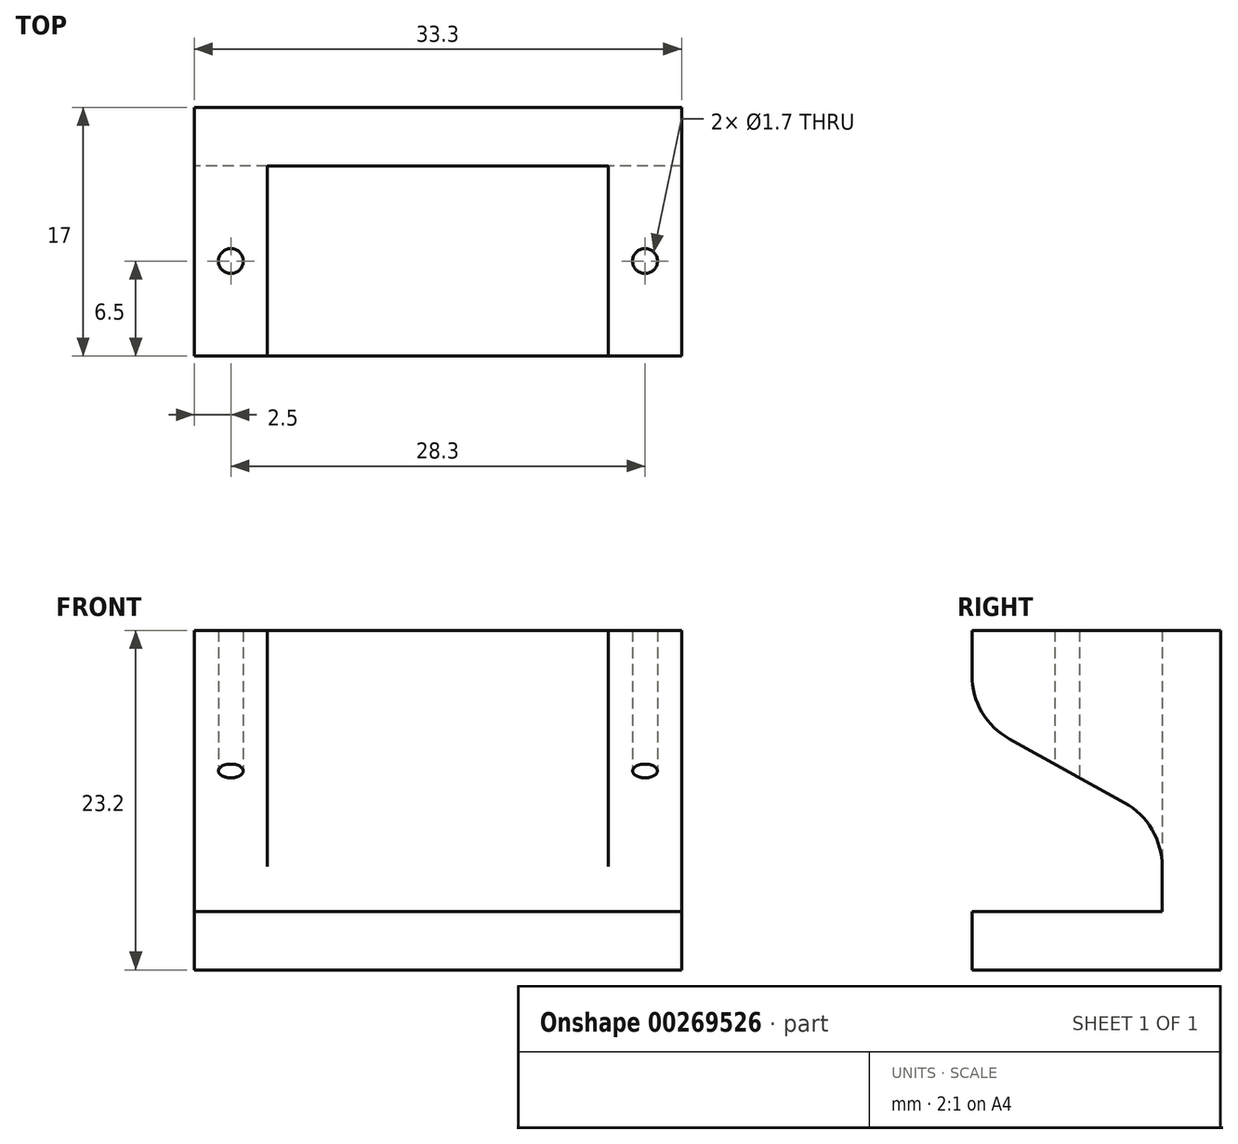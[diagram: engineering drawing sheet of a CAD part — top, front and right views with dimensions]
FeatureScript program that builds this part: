
annotation { "Feature Type Name" : "Feature", "Feature Type Description" : "" }
export const myFeature = defineFeature(function(context is Context, id is Id, definition is map)
    precondition{}
    {
        {
            var Q0;
            Q0=qCreatedBy(makeId("Top.planeOp"),FACE);
            var sketch = newSketch(context, id + "F0", { "sketchPlane" : qUnion([Q0])});
            skLineSegment(sketch, "E0.bottom", {"start": v(16.65, 8.5) * mm, "end": v(-16.65, 8.5) * mm});
            skLineSegment(sketch, "E0.top", {"start": v(16.65, -8.5) * mm, "end": v(-16.65, -8.5) * mm});
            skLineSegment(sketch, "E0.left", {"start": v(16.65, 8.5) * mm, "end": v(16.65, -8.5) * mm});
            skLineSegment(sketch, "E0.right", {"start": v(-16.65, 8.5) * mm, "end": v(-16.65, -8.5) * mm});
            skPoint(sketch, "E0.middle", {"position": v(0, 0) * mm});
            skLineSegment(sketch, "E1", {"start": v(11.65, -8.5) * mm, "end": v(11.65, 8.5) * mm});
            skLineSegment(sketch, "E2", {"start": v(-11.65, -8.5) * mm, "end": v(-11.65, 8.5) * mm});
            skLineSegment(sketch, "E3", {"start": v(-11.65, 4.5) * mm, "end": v(11.65, 4.5) * mm});
            skCircle(sketch, "E4", {"center": v(14.15, -2) * mm, "radius": 0.85 * mm});
            skCircle(sketch, "E5", {"center": v(-14.15, -2) * mm, "radius": 0.85 * mm});
            skCircle(sketch, "E6", {"center": v(-5.75, -2.2) * mm, "radius": 3.8 * mm});
            skCircle(sketch, "E7.MirrorC", {"center": v(5.75, -2.2) * mm, "radius": 3.8 * mm});
            skSolve(sketch);
        }
        {
            var Q0;
            Q0=qCreatedBy(makeId("Front.planeOp"),FACE);
            var sketch = newSketch(context, id + "F1", { "sketchPlane" : qUnion([Q0])});
            skLineSegment(sketch, "E8.bottom", {"start": v(-16.65, 0) * mm, "end": v(16.65, 0) * mm});
            skLineSegment(sketch, "E8.top", {"start": v(-16.65, 23.2) * mm, "end": v(16.65, 23.2) * mm});
            skLineSegment(sketch, "E8.left", {"start": v(-16.65, 0) * mm, "end": v(-16.65, 23.2) * mm});
            skLineSegment(sketch, "E8.right", {"start": v(16.65, 0) * mm, "end": v(16.65, 23.2) * mm});
            skLineSegment(sketch, "E9", {"start": v(-16.65, 4) * mm, "end": v(16.65, 4) * mm});
            skLineSegment(sketch, "E10", {"start": v(11.65, 0) * mm, "end": v(11.65, 23.2) * mm});
            skLineSegment(sketch, "E11", {"start": v(-11.65, 0) * mm, "end": v(-11.65, 23.2) * mm});
            skLineSegment(sketch, "E12", {"start": v(16.65, 10) * mm, "end": v(11.65, 10) * mm});
            skLineSegment(sketch, "E13", {"start": v(-11.65, 10) * mm, "end": v(-16.65, 10) * mm});
            skLineSegment(sketch, "E14", {"start": v(11.65, 17.2) * mm, "end": v(16.65, 17.2) * mm});
            skLineSegment(sketch, "E15", {"start": v(-11.65, 17.2) * mm, "end": v(-16.65, 17.2) * mm});
            skSolve(sketch);
        }
        {
            var Q0;
            Q0=qCreatedBy(makeId("Right.planeOp"),FACE);
            var sketch = newSketch(context, id + "F2", { "sketchPlane" : qUnion([Q0])});
            skLineSegment(sketch, "E16.bottom", {"start": v(-8.5, 0) * mm, "end": v(8.5, 0) * mm});
            skLineSegment(sketch, "E16.top", {"start": v(-8.5, 23.2) * mm, "end": v(8.5, 23.2) * mm});
            skLineSegment(sketch, "E16.left", {"start": v(-8.5, 20.15) * mm, "end": v(-8.5, 23.2) * mm});
            skLineSegment(sketch, "E16.right", {"start": v(8.5, 0) * mm, "end": v(8.5, 23.2) * mm});
            skLineSegment(sketch, "E17", {"start": v(4.5, 7.05) * mm, "end": v(4.5, 0) * mm});
            skLineSegment(sketch, "E18", {"start": v(4.5, 17.2) * mm, "end": v(-8.5, 17.2) * mm});
            skLineSegment(sketch, "E19", {"start": v(4.5, 4) * mm, "end": v(-8.5, 4) * mm});
            skLineSegment(sketch, "E20", {"start": v(-8.5, 10) * mm, "end": v(4.5, 10) * mm});
            skLineSegment(sketch, "E21", {"start": v(-5.92, 15.77) * mm, "end": v(1.92, 11.43) * mm});
            skArc(sketch, "E22.filletArc", {"start": v(-8.5, 20.15) * mm, "mid": v(-7.8, 17.6) * mm, "end": v(-5.92, 15.77) * mm});
            skArc(sketch, "E23.filletArc", {"start": v(4.5, 7.05) * mm, "mid": v(3.8, 9.6) * mm, "end": v(1.92, 11.43) * mm});
            skLineSegment(sketch, "E24", {"start": v(-8.5, 20.15) * mm, "end": v(-8.5, 0) * mm});
            skSolve(sketch);
        }
        {
            var Q0;
            {var subQ0=sQuery(id+"F1.wireOp",EDGE,"E13");Q0=makeQuery(id+"F1.imprint","IMPRINT",FACE,{"disambiguationData":[TD([[makeQuery(id+"F1.imprint","IMPRINT",EDGE,{"derivedFrom":subQ0}),-1.0]])]});}
            var Q1;
            {var subQ5=sQuery(id+"F1.wireOp",EDGE,"E15");Q1=makeQuery(id+"F1.imprint","IMPRINT",FACE,{"disambiguationData":[TD([[makeQuery(id+"F1.imprint","IMPRINT",EDGE,{"derivedFrom":subQ5}),-1.0]])]});}
            var Q2;
            {var subQ3=sQuery(id+"F1.wireOp",EDGE,"E13");Q2=makeQuery(id+"F1.imprint","IMPRINT",FACE,{"disambiguationData":[TD([[makeQuery(id+"F1.imprint","IMPRINT",EDGE,{"derivedFrom":subQ3}),1.0]])]});}
            var Q3;
            {var subQ0=sQuery(id+"F1.wireOp",EDGE,"E8.left");var subQ1=sQuery(id+"F1.wireOp",EDGE,"E8.bottom");var subQ2=makeQuery(id+"F1.imprint","INTERSECT",VERTEX,{"derivedFrom":[subQ1,subQ0]});Q3=makeQuery(id+"F1.imprint","IMPRINT",FACE,{"disambiguationData":[TD([[makeQuery(id+"F1.imprint","IMPRINT",EDGE,{"disambiguationData":[TD([[subQ2,-1.0]])],"derivedFrom":subQ1}),1.0]])]});}
            var Q4;
            {var subQ0=sQuery(id+"F1.wireOp",EDGE,"E10");var subQ1=sQuery(id+"F1.wireOp",EDGE,"E8.bottom");var subQ2=makeQuery(id+"F1.imprint","INTERSECT",VERTEX,{"derivedFrom":[subQ1,subQ0]});Q4=makeQuery(id+"F1.imprint","IMPRINT",FACE,{"disambiguationData":[TD([[makeQuery(id+"F1.imprint","IMPRINT",EDGE,{"disambiguationData":[TD([[subQ2,1.0]])],"derivedFrom":subQ1}),1.0]])]});}
            var Q5;
            {var subQ0=sQuery(id+"F1.wireOp",EDGE,"E8.right");var subQ1=sQuery(id+"F1.wireOp",EDGE,"E8.bottom");var subQ2=makeQuery(id+"F1.imprint","INTERSECT",VERTEX,{"derivedFrom":[subQ1,subQ0]});Q5=makeQuery(id+"F1.imprint","IMPRINT",FACE,{"disambiguationData":[TD([[makeQuery(id+"F1.imprint","IMPRINT",EDGE,{"disambiguationData":[TD([[subQ2,1.0]])],"derivedFrom":subQ1}),1.0]])]});}
            var Q6;
            {var subQ3=sQuery(id+"F1.wireOp",EDGE,"E12");Q6=makeQuery(id+"F1.imprint","IMPRINT",FACE,{"disambiguationData":[TD([[makeQuery(id+"F1.imprint","IMPRINT",EDGE,{"derivedFrom":subQ3}),1.0]])]});}
            var Q7;
            {var subQ0=sQuery(id+"F1.wireOp",EDGE,"E12");Q7=makeQuery(id+"F1.imprint","IMPRINT",FACE,{"disambiguationData":[TD([[makeQuery(id+"F1.imprint","IMPRINT",EDGE,{"derivedFrom":subQ0}),-1.0]])]});}
            var Q8;
            {var subQ5=sQuery(id+"F1.wireOp",EDGE,"E14");Q8=makeQuery(id+"F1.imprint","IMPRINT",FACE,{"disambiguationData":[TD([[makeQuery(id+"F1.imprint","IMPRINT",EDGE,{"derivedFrom":subQ5}),1.0]])]});}
            extrude(context, id + "F3", {"entities" : qUnion([Q0, Q1, Q2, Q3, Q4, Q5, Q6, Q7, Q8]), "endBound" : BoundingType.SYMMETRIC, "depth" : 17 * mm});
        }
        {
            var Q0;
            {var subQ5=sQuery(id+"F0.wireOp",EDGE,"E3");Q0=makeQuery(id+"F0.imprint","IMPRINT",FACE,{"disambiguationData":[TD([[makeQuery(id+"F0.imprint","IMPRINT",EDGE,{"derivedFrom":subQ5}),1.0]])]});}
            extrude(context, id + "F4", {"entities" : qUnion([Q0]), "operationType" : NewBodyOperationType.ADD, "depth" : 23.2 * mm});
        }
        {
            var Q0;
            {var subQ0=sQuery(id+"F2.wireOp",EDGE,"E21");Q0=makeQuery(id+"F2.imprint","IMPRINT",FACE,{"disambiguationData":[TD([[makeQuery(id+"F2.imprint","IMPRINT",EDGE,{"derivedFrom":subQ0}),-1.0]])]});}
            var Q1;
            {var subQ0=sQuery(id+"F2.wireOp",EDGE,"E24");var subQ1=sQuery(id+"F2.wireOp",EDGE,"E18");var subQ2=makeQuery(id+"F2.imprint","INTERSECT",VERTEX,{"derivedFrom":[subQ1,subQ0]});Q1=makeQuery(id+"F2.imprint","IMPRINT",FACE,{"disambiguationData":[TD([[makeQuery(id+"F2.imprint","IMPRINT",EDGE,{"disambiguationData":[TD([[subQ2,1.0]])],"derivedFrom":subQ1}),-1.0]])]});}
            var Q2;
            {var subQ5=sQuery(id+"F2.wireOp",EDGE,"E19");Q2=makeQuery(id+"F2.imprint","IMPRINT",FACE,{"disambiguationData":[TD([[makeQuery(id+"F2.imprint","IMPRINT",EDGE,{"derivedFrom":subQ5}),-1.0]])]});}
            extrude(context, id + "F5", {"entities" : qUnion([Q0, Q1, Q2]), "operationType" : NewBodyOperationType.REMOVE, "endBound" : BoundingType.SYMMETRIC, "oppositeDirection" : true, "depth" : 36.2 * mm});
        }
        {
            var Q0;
            Q0=makeQuery(id+"F0.imprint","IMPRINT",FACE,{"disambiguationData":[TD([[makeQuery(id+"F0.imprint","IMPRINT",EDGE,{"derivedFrom":sQuery(id+"F0.wireOp",EDGE,"E4")}),1.0]])]});
            var Q1;
            Q1=makeQuery(id+"F0.imprint","IMPRINT",FACE,{"disambiguationData":[TD([[makeQuery(id+"F0.imprint","IMPRINT",EDGE,{"derivedFrom":sQuery(id+"F0.wireOp",EDGE,"E5")}),1.0]])]});
            extrude(context, id + "F6", {"entities" : qUnion([Q0, Q1]), "operationType" : NewBodyOperationType.REMOVE, "depth" : 25 * mm, "hasSecondDirection" : true, "secondDirectionOppositeDirection" : false, "secondDirectionDepth" : 4.3 * mm});
        }
    });
